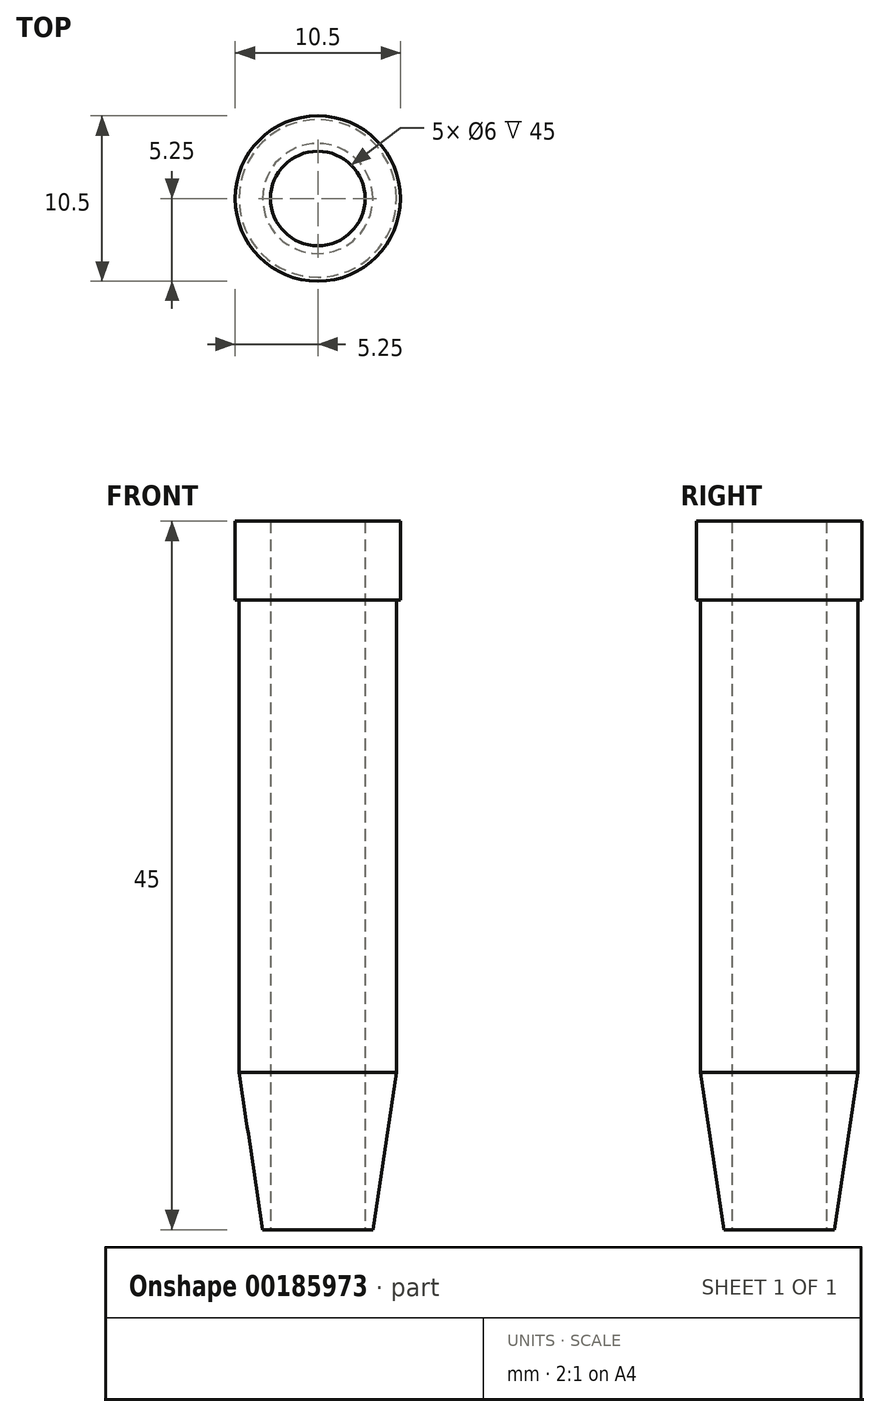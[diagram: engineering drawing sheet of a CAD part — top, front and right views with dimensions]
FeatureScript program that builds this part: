
annotation { "Feature Type Name" : "Feature", "Feature Type Description" : "" }
export const myFeature = defineFeature(function(context is Context, id is Id, definition is map)
    precondition{}
    {
        {
            var Q0;
            Q0=qCreatedBy(makeId("Front.planeOp"),FACE);
            var sketch = newSketch(context, id + "F0", { "sketchPlane" : qUnion([Q0])});
            skLineSegment(sketch, "E0", {"start": v(0, 0) * mm, "end": v(0, 45) * mm, "construction": true});
            skLineSegment(sketch, "E1", {"start": v(3, 0) * mm, "end": v(3, 45) * mm});
            skLineSegment(sketch, "E2", {"start": v(3, 0) * mm, "end": v(3.5, 0) * mm});
            skLineSegment(sketch, "E3", {"start": v(3.5, 0) * mm, "end": v(5, 10) * mm});
            skLineSegment(sketch, "E4", {"start": v(5, 10) * mm, "end": v(5, 40) * mm});
            skLineSegment(sketch, "E5", {"start": v(5, 40) * mm, "end": v(5.25, 40) * mm});
            skLineSegment(sketch, "E6", {"start": v(5.25, 40) * mm, "end": v(5.25, 45) * mm});
            skLineSegment(sketch, "E7", {"start": v(5.25, 45) * mm, "end": v(3, 45) * mm});
            skSolve(sketch);
        }
        {
            var Q0;
            Q0=makeQuery(id+"F0.imprint","IMPRINT",FACE,{"disambiguationData":[TD([[makeQuery(id+"F0.imprint","IMPRINT",EDGE,{"derivedFrom":sQuery(id+"F0.wireOp",EDGE,"E1")}),-1.0]])]});
            var Q1;
            Q1=sQuery(id+"F0.wireOp",EDGE,"E0");
            revolve(context, id + "F1", {"entities" : qUnion([Q0]), "axis" : qUnion([Q1]), "revolveType" : RevolveType.FULL});
        }
    });
